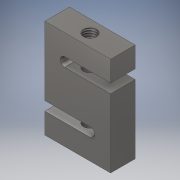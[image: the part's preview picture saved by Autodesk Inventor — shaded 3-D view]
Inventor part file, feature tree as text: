
AUTODESK INVENTOR PART (.ipt)
format: ipt  version: 2019.4 (Build 234330000, 330)  size: 140,800 bytes
history: native  units: mm
features: sketch x2, extrude x1, hole x1
ambient origin geometry x8: Origin, YZ Plane, XZ Plane, XY Plane, X Axis, Y Axis, Z Axis, Center Point
bodies: Solid1 (feature_tree)
feature tree (4):
  extrude  "Extrusion1"  Depth=76.2mm
  hole  "Hole1"  [1 undecoded]
  sketch  "Sketch1"  dims[d0=50.8mm d1=76.2mm]
  sketch  "Sketch2"  dims[d2=50.8mm d3=16.0mm d4=16.0mm d5=30.0mm d6=12.0mm d7=12.0mm d8=7.1mm d9=7.1mm d10=19.0mm d11=0.0mm d12=10.106mm d13=24.0mm d14=4.0mm d15=2.0mm d16=90.0deg d17=32.3mm d18=20.594885mm]
note: 1 required parameter value undecoded (feature->parameter linkage not recoverable at this tier; creation-order binding heuristic only, values carry confidence <= 0.55)
